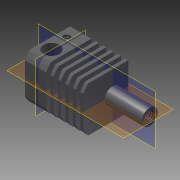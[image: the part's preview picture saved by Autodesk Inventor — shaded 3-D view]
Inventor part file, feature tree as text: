
AUTODESK INVENTOR PART (.ipt)
format: ipt  version: 2015 (Build 190159000, 159)  size: 231,936 bytes
history: native  units: mm
features: hole x3, extrude x2, revolve x1, plane x1, mirror x1, sketch x1
ambient origin geometry x8: Origin, YZ Plane, XZ Plane, XY Plane, X Axis, Y Axis, Z Axis, Center Point
bodies: Solid1 (feature_tree)
feature tree (9):
  revolve  "Revolución1"  [1 undecoded]
  extrude  "Extrusión1"  Depth=10.0mm
  extrude  "Extrusión2"  Depth=10.0mm
  hole  "Agujero1"  [1 undecoded]
  hole  "Agujero2"  [1 undecoded]
  hole  "Agujero4"  [1 undecoded]
  plane  "Plano de trabajo1"
  mirror  "Simetría1"
  sketch  "Boceto3"  dims[d0=48.0mm d1=0.8mm d2=4.0mm d5=6.0mm d6=2.5mm d7=30.0deg d8=45.0deg d9=8.0mm d10=0.4mm d11=0.5mm d12=2.0mm d13=45.0deg d15=11.0mm d16=5.0mm d17=6.0mm d18=4.0mm d19=8.0mm d21=4.0mm d26=90.0deg d27=17.0mm d28=17.0mm d29=8.5mm d30=6.0mm d31=10.0mm d32=0.0mm d33=10.0mm d34=0.0mm d36=4.0mm d37=2.0mm d39=0.85mm d40=30.0deg d42=2.459mm d43=5.0mm d44=4.0mm d45=2.0mm d46=90.0deg d47=6.0mm d48=20.594885mm d49=25.0mm d50=25.0mm d51=22.0mm d52=1.6mm d53=1.2mm d54=1.0mm d55=1.2mm d57=1.6mm d58=1.2mm d64=8.0mm d65=6.0mm d66=1.0mm d67=4.0mm d68=4.0mm d69=10.0mm d70=10.0mm d71=4.134mm d72=6.0mm d73=4.0mm d74=2.0mm d75=90.0deg d76=6.5mm d77=0.0mm d88=1.2mm d89=1.2mm d90=2.459mm d91=6.0mm d92=4.0mm d93=2.0mm d94=90.0deg d95=5.0mm d96=20.594885mm d97=-5.0mm d100=2.75mm d101=7.0mm d102=1.6mm d103=0.494975mm d104=0.7mm]
note: 4 required parameter values undecoded (feature->parameter linkage not recoverable at this tier; creation-order binding heuristic only, values carry confidence <= 0.55)